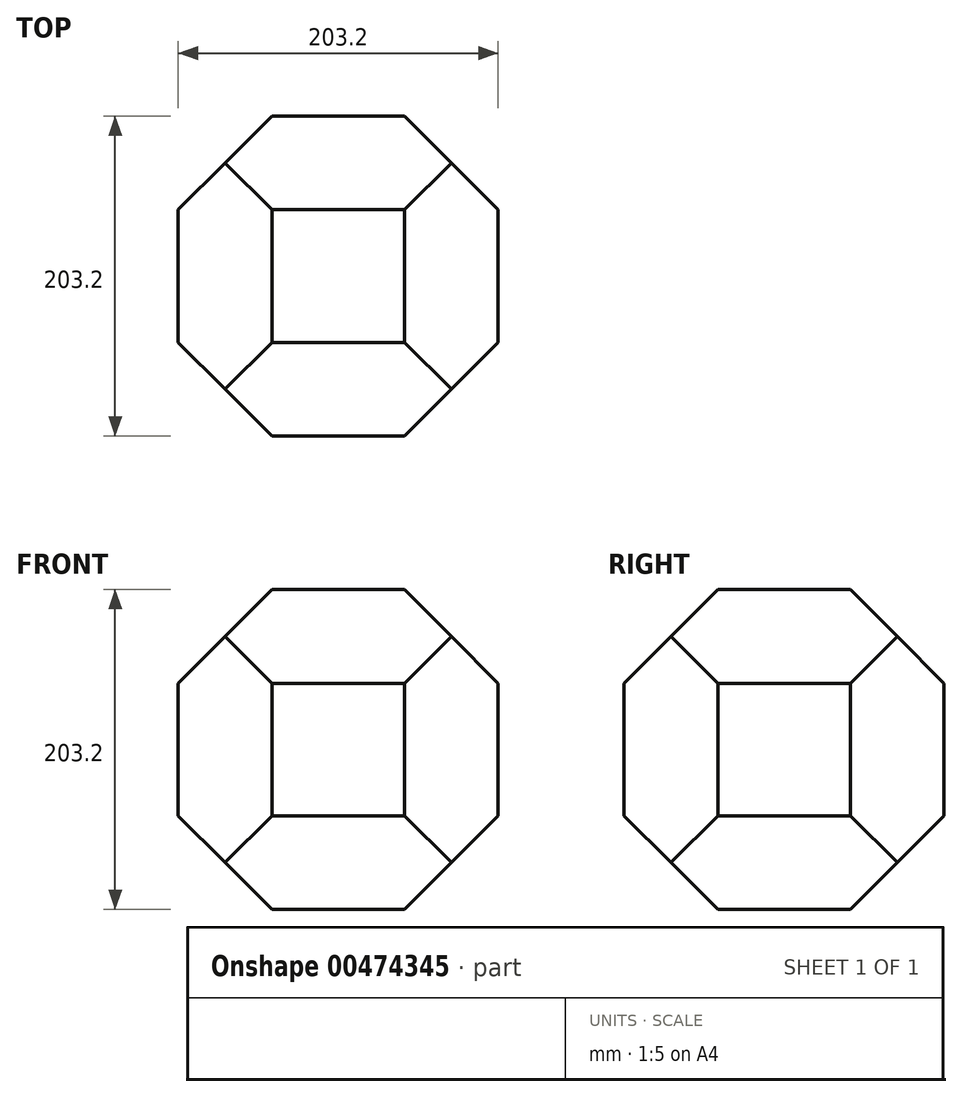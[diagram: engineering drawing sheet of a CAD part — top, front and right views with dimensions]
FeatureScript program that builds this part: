
annotation { "Feature Type Name" : "Feature", "Feature Type Description" : "" }
export const myFeature = defineFeature(function(context is Context, id is Id, definition is map)
    precondition{}
    {
        {
            var Q0;
            Q0=qCreatedBy(makeId("Front.planeOp"),FACE);
            var sketch = newSketch(context, id + "F0", { "sketchPlane" : qUnion([Q0])});
            skLineSegment(sketch, "E0.bottom", {"start": v(-101.6, 101.6) * mm, "end": v(101.6, 101.6) * mm});
            skLineSegment(sketch, "E0.top", {"start": v(-101.6, -101.6) * mm, "end": v(101.6, -101.6) * mm});
            skLineSegment(sketch, "E0.left", {"start": v(-101.6, 101.6) * mm, "end": v(-101.6, -101.6) * mm});
            skLineSegment(sketch, "E0.right", {"start": v(101.6, 101.6) * mm, "end": v(101.6, -101.6) * mm});
            skSolve(sketch);
        }
        {
            var Q0;
            Q0=makeQuery(id+"F0.imprint","IMPRINT",FACE,{"disambiguationData":[TD([[makeQuery(id+"F0.imprint","IMPRINT",EDGE,{"derivedFrom":sQuery(id+"F0.wireOp",EDGE,"E0.bottom")}),-1.0]])]});
            extrude(context, id + "F1", {"entities" : qUnion([Q0]), "endBound" : BoundingType.SYMMETRIC, "depth" : 203.2 * mm});
        }
        {
            var Q0;
            Q0=makeQuery(id+"F1.opExtrude","SWEPT_FACE",FACE,{"disambiguationData":[OSD([sQuery(id+"F0.wireOp",EDGE,"E0.bottom")])]});
            var sketch = newSketch(context, id + "F2", { "sketchPlane" : qUnion([Q0])});
            skLineSegment(sketch, "E1", {"start": v(-42.08, 101.6) * mm, "end": v(-101.6, 101.6) * mm});
            skLineSegment(sketch, "E2", {"start": v(-101.6, 101.6) * mm, "end": v(-101.6, 42.08) * mm});
            skLineSegment(sketch, "E3", {"start": v(-101.6, 42.08) * mm, "end": v(-42.08, 101.6) * mm});
            skLineSegment(sketch, "E4", {"start": v(0, 0) * mm, "end": v(0, 101.6) * mm});
            skLineSegment(sketch, "E5.MirrorCS", {"start": v(101.6, 101.6) * mm, "end": v(101.6, 42.08) * mm});
            skLineSegment(sketch, "E6.MirrorCS", {"start": v(42.08, 101.6) * mm, "end": v(101.6, 101.6) * mm});
            skLineSegment(sketch, "E7.MirrorCS", {"start": v(101.6, 42.08) * mm, "end": v(42.08, 101.6) * mm});
            skLineSegment(sketch, "E8", {"start": v(101.6, 0) * mm, "end": v(-101.6, 0) * mm});
            skLineSegment(sketch, "E9.MirrorCS", {"start": v(-101.6, -101.6) * mm, "end": v(-101.6, -42.08) * mm});
            skLineSegment(sketch, "E10.MirrorCS", {"start": v(-101.6, -42.08) * mm, "end": v(-42.08, -101.6) * mm});
            skLineSegment(sketch, "E11.MirrorCS", {"start": v(-42.08, -101.6) * mm, "end": v(-101.6, -101.6) * mm});
            skLineSegment(sketch, "E12.MirrorCS", {"start": v(101.6, -42.08) * mm, "end": v(42.08, -101.6) * mm});
            skLineSegment(sketch, "E13.MirrorCS", {"start": v(42.08, -101.6) * mm, "end": v(101.6, -101.6) * mm});
            skLineSegment(sketch, "E14.MirrorCS", {"start": v(101.6, -101.6) * mm, "end": v(101.6, -42.08) * mm});
            skLineSegment(sketch, "E15", {"start": v(-42.08, 101.6) * mm, "end": v(42.08, 101.6) * mm});
            skLineSegment(sketch, "E16", {"start": v(101.6, 42.08) * mm, "end": v(101.6, -42.08) * mm});
            skLineSegment(sketch, "E17", {"start": v(42.08, -101.6) * mm, "end": v(-42.08, -101.6) * mm});
            skLineSegment(sketch, "E18", {"start": v(-101.6, -42.08) * mm, "end": v(-101.6, 42.08) * mm});
            skSolve(sketch);
        }
        {
            var Q0;
            Q0=makeQuery(id+"F2.imprint","IMPRINT",FACE,{"disambiguationData":[TD([[makeQuery(id+"F2.imprint","IMPRINT",EDGE,{"derivedFrom":sQuery(id+"F2.wireOp",EDGE,"E1")}),-1.0]])]});
            var Q1;
            Q1=makeQuery(id+"F2.imprint","IMPRINT",FACE,{"disambiguationData":[TD([[makeQuery(id+"F2.imprint","IMPRINT",EDGE,{"derivedFrom":sQuery(id+"F2.wireOp",EDGE,"E5.MirrorCS")}),1.0]])]});
            var Q2;
            Q2=makeQuery(id+"F2.imprint","IMPRINT",FACE,{"disambiguationData":[TD([[makeQuery(id+"F2.imprint","IMPRINT",EDGE,{"derivedFrom":sQuery(id+"F2.wireOp",EDGE,"E12.MirrorCS")}),1.0]])]});
            var Q3;
            Q3=makeQuery(id+"F2.imprint","IMPRINT",FACE,{"disambiguationData":[TD([[makeQuery(id+"F2.imprint","IMPRINT",EDGE,{"derivedFrom":sQuery(id+"F2.wireOp",EDGE,"E9.MirrorCS")}),-1.0]])]});
            extrude(context, id + "F3", {"entities" : qUnion([Q0, Q1, Q2, Q3]), "operationType" : NewBodyOperationType.REMOVE, "oppositeDirection" : true, "depth" : 203.2 * mm});
        }
        {
            var Q0;
            Q0=qCreatedBy(makeId("Front.planeOp"),FACE);
            var sketch = newSketch(context, id + "F4", { "sketchPlane" : qUnion([Q0])});
            skPoint(sketch, "E19.middle", {"position": v(0, 0) * mm});
            skLineSegment(sketch, "E20", {"start": v(-42.08, 101.6) * mm, "end": v(-101.6, 101.6) * mm});
            skLineSegment(sketch, "E21", {"start": v(-101.6, 42.08) * mm, "end": v(-42.08, 101.6) * mm});
            skLineSegment(sketch, "E22", {"start": v(42.08, 101.6) * mm, "end": v(101.6, 101.6) * mm});
            skLineSegment(sketch, "E23", {"start": v(101.6, 42.08) * mm, "end": v(42.08, 101.6) * mm});
            skLineSegment(sketch, "E24", {"start": v(101.6, -42.08) * mm, "end": v(101.6, -101.6) * mm});
            skLineSegment(sketch, "E25", {"start": v(42.08, -101.6) * mm, "end": v(101.6, -42.08) * mm});
            skLineSegment(sketch, "E26", {"start": v(-42.08, -101.6) * mm, "end": v(-101.6, -101.6) * mm});
            skLineSegment(sketch, "E27", {"start": v(-101.6, -42.08) * mm, "end": v(-42.08, -101.6) * mm});
            skLineSegment(sketch, "E28", {"start": v(-101.6, 42.08) * mm, "end": v(-101.6, 101.6) * mm});
            skLineSegment(sketch, "E29", {"start": v(101.6, 42.08) * mm, "end": v(101.6, 101.6) * mm});
            skLineSegment(sketch, "E30", {"start": v(-101.6, -42.08) * mm, "end": v(-101.6, -101.6) * mm});
            skLineSegment(sketch, "E31", {"start": v(101.6, -101.6) * mm, "end": v(42.08, -101.6) * mm});
            skLineSegment(sketch, "E32", {"start": v(-42.08, 101.6) * mm, "end": v(42.08, 101.6) * mm});
            skSolve(sketch);
        }
        {
            var Q0;
            Q0=makeQuery(id+"F4.imprint","IMPRINT",FACE,{"disambiguationData":[TD([[makeQuery(id+"F4.imprint","IMPRINT",EDGE,{"derivedFrom":sQuery(id+"F4.wireOp",EDGE,"E20")}),1.0]])]});
            var Q1;
            Q1=makeQuery(id+"F4.imprint","IMPRINT",FACE,{"disambiguationData":[TD([[makeQuery(id+"F4.imprint","IMPRINT",EDGE,{"derivedFrom":sQuery(id+"F4.wireOp",EDGE,"E26")}),-1.0]])]});
            var Q2;
            Q2=makeQuery(id+"F4.imprint","IMPRINT",FACE,{"disambiguationData":[TD([[makeQuery(id+"F4.imprint","IMPRINT",EDGE,{"derivedFrom":sQuery(id+"F4.wireOp",EDGE,"E24")}),-1.0]])]});
            var Q3;
            Q3=makeQuery(id+"F4.imprint","IMPRINT",FACE,{"disambiguationData":[TD([[makeQuery(id+"F4.imprint","IMPRINT",EDGE,{"derivedFrom":sQuery(id+"F4.wireOp",EDGE,"E22")}),-1.0]])]});
            extrude(context, id + "F5", {"entities" : qUnion([Q0, Q1, Q2, Q3]), "operationType" : NewBodyOperationType.REMOVE, "endBound" : BoundingType.SYMMETRIC, "oppositeDirection" : true, "depth" : 203.2 * mm});
        }
        {
            var Q0;
            Q0=qCreatedBy(makeId("Right.planeOp"),FACE);
            var sketch = newSketch(context, id + "F6", { "sketchPlane" : qUnion([Q0])});
            skLineSegment(sketch, "E33", {"start": v(42.08, 101.6) * mm, "end": v(101.6, 101.6) * mm});
            skLineSegment(sketch, "E34", {"start": v(101.6, 101.6) * mm, "end": v(101.6, 42.08) * mm});
            skLineSegment(sketch, "E35", {"start": v(101.6, 42.08) * mm, "end": v(42.08, 101.6) * mm});
            skLineSegment(sketch, "E36", {"start": v(101.6, -42.08) * mm, "end": v(101.6, -101.6) * mm});
            skLineSegment(sketch, "E37", {"start": v(101.6, -101.6) * mm, "end": v(42.08, -101.6) * mm});
            skLineSegment(sketch, "E38", {"start": v(42.08, -101.6) * mm, "end": v(101.6, -42.08) * mm});
            skLineSegment(sketch, "E39", {"start": v(-42.08, -101.6) * mm, "end": v(-101.6, -101.6) * mm});
            skLineSegment(sketch, "E40", {"start": v(-101.6, -101.6) * mm, "end": v(-101.6, -42.08) * mm});
            skLineSegment(sketch, "E41", {"start": v(-101.6, -42.08) * mm, "end": v(-42.08, -101.6) * mm});
            skLineSegment(sketch, "E42", {"start": v(-42.08, 101.6) * mm, "end": v(-101.6, 101.6) * mm});
            skLineSegment(sketch, "E43", {"start": v(-101.6, 101.6) * mm, "end": v(-101.6, 42.08) * mm});
            skLineSegment(sketch, "E44", {"start": v(-101.6, 42.08) * mm, "end": v(-42.08, 101.6) * mm});
            skLineSegment(sketch, "E45", {"start": v(-42.08, 101.6) * mm, "end": v(42.08, 101.6) * mm});
            skSolve(sketch);
        }
        {
            var Q0;
            Q0=makeQuery(id+"F6.imprint","IMPRINT",FACE,{"disambiguationData":[TD([[makeQuery(id+"F6.imprint","IMPRINT",EDGE,{"derivedFrom":sQuery(id+"F6.wireOp",EDGE,"E33")}),-1.0]])]});
            var Q1;
            Q1=makeQuery(id+"F6.imprint","IMPRINT",FACE,{"disambiguationData":[TD([[makeQuery(id+"F6.imprint","IMPRINT",EDGE,{"derivedFrom":sQuery(id+"F6.wireOp",EDGE,"E36")}),-1.0]])]});
            var Q2;
            Q2=makeQuery(id+"F6.imprint","IMPRINT",FACE,{"disambiguationData":[TD([[makeQuery(id+"F6.imprint","IMPRINT",EDGE,{"derivedFrom":sQuery(id+"F6.wireOp",EDGE,"E39")}),-1.0]])]});
            var Q3;
            Q3=makeQuery(id+"F6.imprint","IMPRINT",FACE,{"disambiguationData":[TD([[makeQuery(id+"F6.imprint","IMPRINT",EDGE,{"derivedFrom":sQuery(id+"F6.wireOp",EDGE,"E42")}),1.0]])]});
            extrude(context, id + "F7", {"entities" : qUnion([Q0, Q1, Q2, Q3]), "operationType" : NewBodyOperationType.REMOVE, "endBound" : BoundingType.SYMMETRIC, "oppositeDirection" : true, "depth" : 203.2 * mm});
        }
    });
